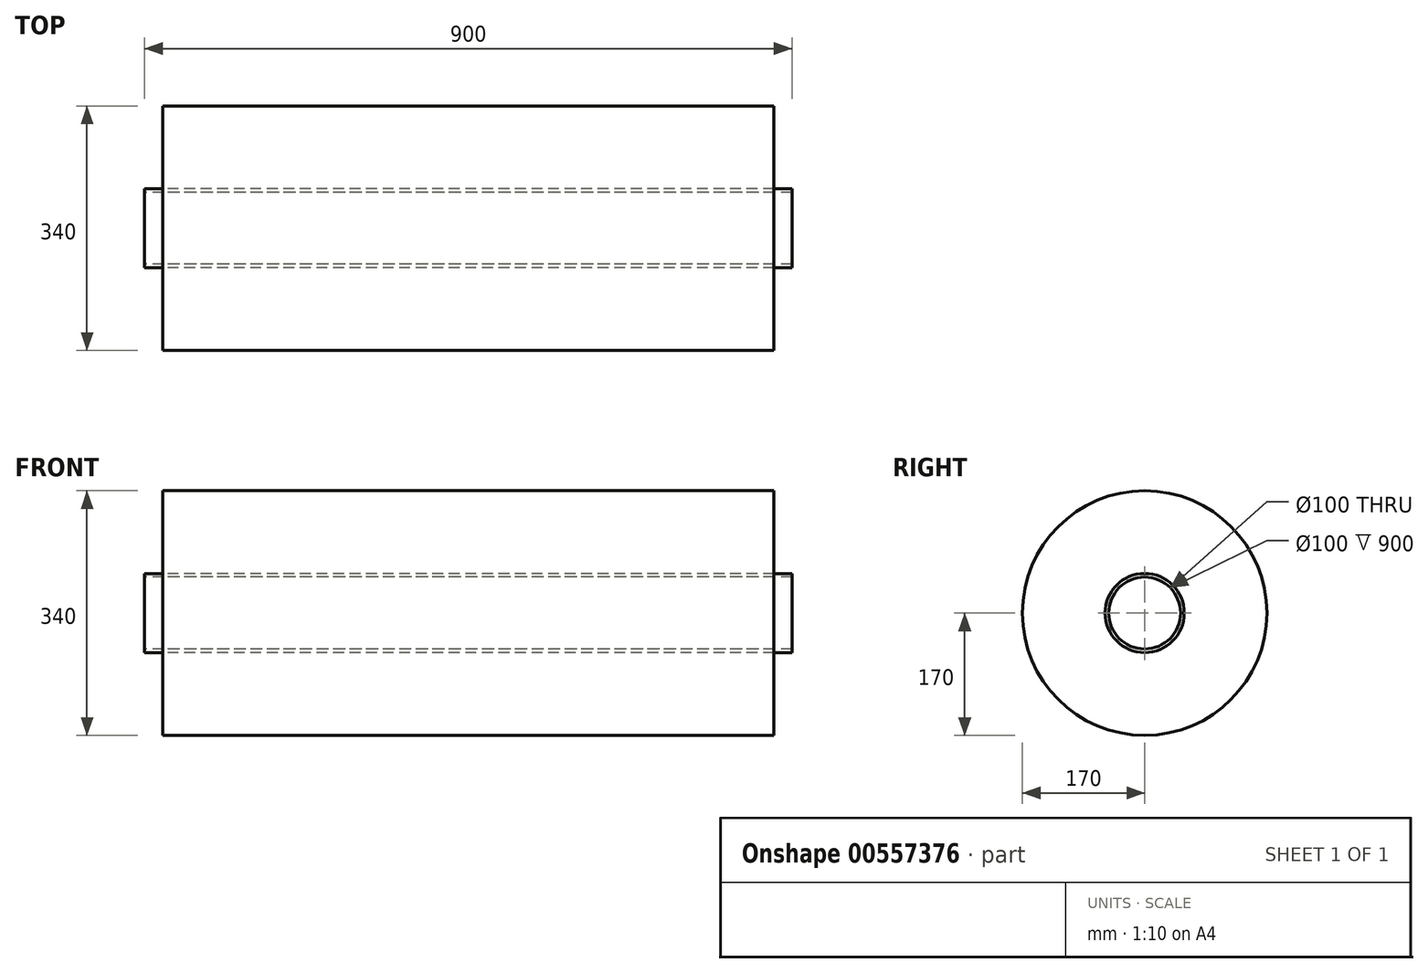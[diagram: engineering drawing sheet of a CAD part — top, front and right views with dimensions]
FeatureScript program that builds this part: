
annotation { "Feature Type Name" : "Feature", "Feature Type Description" : "" }
export const myFeature = defineFeature(function(context is Context, id is Id, definition is map)
    precondition{}
    {
        {
            var Q0;
            Q0=qCreatedBy(makeId("Right.planeOp"),FACE);
            var sketch = newSketch(context, id + "F0", { "sketchPlane" : qUnion([Q0])});
            skCircle(sketch, "E0", {"center": v(0, 0) * mm, "radius": 170 * mm});
            skCircle(sketch, "E1", {"center": v(0, 0) * mm, "radius": 50 * mm});
            skSolve(sketch);
        }
        {
            var Q0;
            Q0=makeQuery(id+"F0.imprint","IMPRINT",FACE,{"disambiguationData":[TD([[makeQuery(id+"F0.imprint","IMPRINT",EDGE,{"derivedFrom":sQuery(id+"F0.wireOp",EDGE,"E0")}),1.0]])]});
            var sketch = newSketch(context, id + "F1", { "sketchPlane" : qUnion([Q0])});
            skCircle(sketch, "E2", {"center": v(0, 0) * mm, "radius": 50 * mm});
            skCircle(sketch, "E3", {"center": v(0, 0) * mm, "radius": 55 * mm});
            skSolve(sketch);
        }
        {
            var Q0;
            Q0 = qSketchRegion(id + "F0", true);
            extrude(context, id + "F2", {"entities" : qUnion([Q0]), "endBound" : BoundingType.SYMMETRIC, "depth" : 850 * mm, "offsetDistance" : 25 * mm});
        }
        {
            var Q0;
            Q0 = qSketchRegion(id + "F1", true);
            extrude(context, id + "F3", {"entities" : qUnion([Q0]), "endBound" : BoundingType.SYMMETRIC, "depth" : 900 * mm, "offsetDistance" : 25 * mm});
        }
    });
